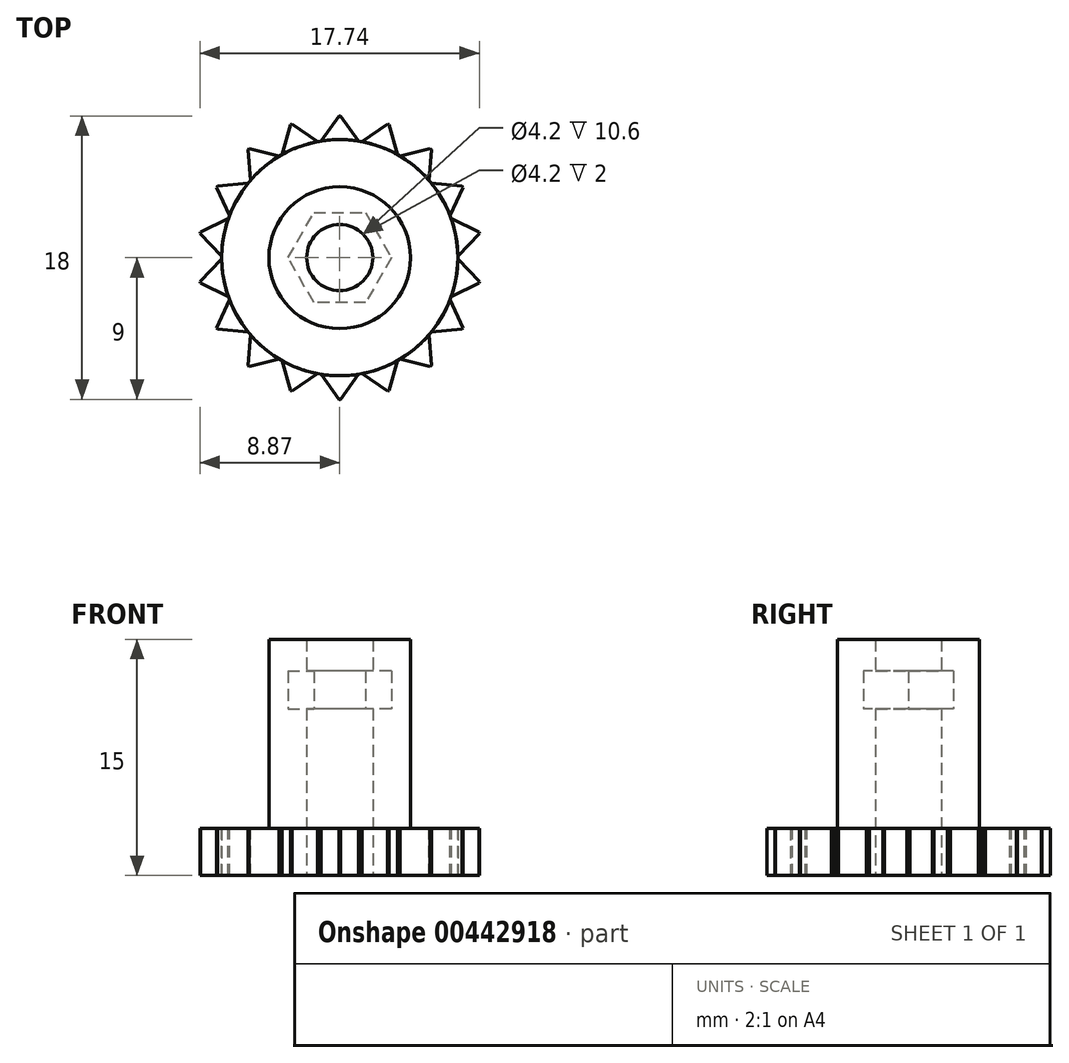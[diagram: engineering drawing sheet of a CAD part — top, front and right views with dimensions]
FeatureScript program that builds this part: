
annotation { "Feature Type Name" : "Feature", "Feature Type Description" : "" }
export const myFeature = defineFeature(function(context is Context, id is Id, definition is map)
    precondition{}
    {
        {
            var Q0;
            Q0=qCreatedBy(makeId("Top.planeOp"),FACE);
            var sketch = newSketch(context, id + "F0", { "sketchPlane" : qUnion([Q0])});
            skCircle(sketch, "E0", {"center": v(0, 0) * mm, "radius": 7.5 * mm});
            skCircle(sketch, "E1", {"center": v(0, 0) * mm, "radius": 4.5 * mm});
            skCircle(sketch, "E2.cCircle", {"center": v(0, 0) * mm, "radius": 2.85 * mm, "construction": true});
            skLineSegment(sketch, "E2.0", {"start": v(1.65, -2.85) * mm, "end": v(-1.65, -2.85) * mm});
            skLineSegment(sketch, "E2.1", {"start": v(-1.65, -2.85) * mm, "end": v(-3.3, 0) * mm});
            skLineSegment(sketch, "E2.2", {"start": v(-3.3, 0) * mm, "end": v(-1.65, 2.85) * mm});
            skLineSegment(sketch, "E2.3", {"start": v(-1.65, 2.85) * mm, "end": v(1.65, 2.85) * mm});
            skLineSegment(sketch, "E2.4", {"start": v(1.65, 2.85) * mm, "end": v(3.3, 0) * mm});
            skLineSegment(sketch, "E2.5", {"start": v(3.3, 0) * mm, "end": v(1.65, -2.85) * mm});
            skPoint(sketch, "E2.0.midPoint", {"position": v(0, -2.85) * mm});
            skCircle(sketch, "E3", {"center": v(0, 0) * mm, "radius": 2.1 * mm});
            skSolve(sketch);
        }
        {
            var Q0;
            Q0=makeQuery(id+"F0.imprint","IMPRINT",FACE,{"disambiguationData":[TD([[makeQuery(id+"F0.imprint","IMPRINT",EDGE,{"derivedFrom":sQuery(id+"F0.wireOp",EDGE,"E1")}),1.0]])]});
            var Q1;
            Q1=makeQuery(id+"F0.imprint","IMPRINT",FACE,{"disambiguationData":[TD([[makeQuery(id+"F0.imprint","IMPRINT",EDGE,{"derivedFrom":sQuery(id+"F0.wireOp",EDGE,"E2.0")}),-1.0]])]});
            extrude(context, id + "F1", {"entities" : qUnion([Q0, Q1]), "depth" : 15 * mm, "offsetDistance" : 25 * mm});
        }
        {
            var Q0;
            Q0=makeQuery(id+"F0.imprint","IMPRINT",FACE,{"disambiguationData":[TD([[makeQuery(id+"F0.imprint","IMPRINT",EDGE,{"derivedFrom":sQuery(id+"F0.wireOp",EDGE,"E0")}),1.0]])]});
            extrude(context, id + "F2", {"entities" : qUnion([Q0]), "operationType" : NewBodyOperationType.ADD, "depth" : 3 * mm});
        }
        {
            var Q0;
            Q0=makeQuery(id+"F0.imprint","IMPRINT",FACE,{"disambiguationData":[TD([[makeQuery(id+"F0.imprint","IMPRINT",EDGE,{"derivedFrom":sQuery(id+"F0.wireOp",EDGE,"E2.0")}),-1.0]])]});
            extrude(context, id + "F3", {"entities" : qUnion([Q0]), "operationType" : NewBodyOperationType.REMOVE, "depth" : 13 * mm, "hasSecondDirection" : true, "secondDirectionOppositeDirection" : false, "secondDirectionDepth" : 10.6 * mm, "offsetDistance" : 25 * mm});
        }
        {
            var Q0;
            Q0=makeQuery(id+"F2.opExtrude","CAP_FACE",FACE,{"disambiguationData":[OSD([sQuery(id+"F0.wireOp",EDGE,"E0"),sQuery(id+"F0.wireOp",EDGE,"E1")])],"isStart":false});
            var sketch = newSketch(context, id + "F4", { "sketchPlane" : qUnion([Q0])});
            skCircle(sketch, "E4.0", {"center": v(0, 0) * mm, "radius": 7.5 * mm});
            skLineSegment(sketch, "E5", {"start": v(-1.2, -7.4) * mm, "end": v(-0.05, -9) * mm});
            skLineSegment(sketch, "E6", {"start": v(-0.05, -9) * mm, "end": v(0.05, -9) * mm});
            skLineSegment(sketch, "E7", {"start": v(0.05, -9) * mm, "end": v(1.2, -7.4) * mm});
            skPoint(sketch, "E8", {"position": v(0, -9) * mm});
            skLineSegment(sketch, "E9", {"start": v(0, -9.03) * mm, "end": v(0, -7.2) * mm, "construction": true});
            skSolve(sketch);
        }
        {
            var Q0;
            {var subQ0=sQuery(id+"F4.wireOp",EDGE,"xMfUHdH3-sUiR-HnJx-IQe0-Awc9sF2Xy2mM");Q0=makeQuery(id+"F4.imprint","IMPRINT",FACE,{"disambiguationData":[TD([[makeQuery(id+"F4.imprint","IMPRINT",EDGE,{"derivedFrom":subQ0}),1.0]])]});}
            var Q1;
            {var subQ0=sQuery(id+"F4.wireOp",EDGE,"E5");Q1=makeQuery(id+"F4.imprint","IMPRINT",FACE,{"disambiguationData":[TD([[makeQuery(id+"F4.imprint","IMPRINT",EDGE,{"derivedFrom":subQ0}),1.0]])]});}
            var Q2;
            {var subQ0=sQuery(id+"F0.wireOp",EDGE,"E1");Q2=makeQuery(id+"F2.boolean.opBoolean","MERGE",FACE,{"derivedFrom":[makeQuery(id+"F1.opExtrude","CAP_FACE",FACE,{"disambiguationData":[OSD([subQ0,sQuery(id+"F0.wireOp",EDGE,"E3")])],"isStart":true}),makeQuery(id+"F2.opExtrude","CAP_FACE",FACE,{"disambiguationData":[OSD([sQuery(id+"F0.wireOp",EDGE,"E0"),subQ0])],"isStart":true})]});}
            extrude(context, id + "F5", {"entities" : qUnion([Q0, Q1]), "endBound" : BoundingType.UP_TO_SURFACE, "oppositeDirection" : true, "endBoundEntityFace" : qUnion([Q2]), "depth" : 25 * mm});
        }
        {
            var Q0;
            Q0=makeQuery(id+"F5.opExtrude","SWEPT_BODY",BODY,{"disambiguationData":[OSD([sQuery(id+"F4.wireOp",EDGE,"E4.0"),sQuery(id+"F4.wireOp",EDGE,"xMfUHdH3-sUiR-HnJx-IQe0-Awc9sF2Xy2mM")])]});
            var Q1;
            Q1=makeQuery(id+"F2.opExtrude","SWEPT_FACE",FACE,{"disambiguationData":[OSD([sQuery(id+"F0.wireOp",EDGE,"E0")])]});
            circularPattern(context, id + "F6", {"entities" : qUnion([Q0]), "axis" : qUnion([Q1]), "angle" : 360 * degree, "instanceCount" : 18, "equalSpace" : true});
        }
    });
